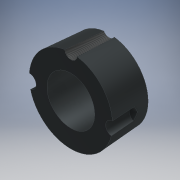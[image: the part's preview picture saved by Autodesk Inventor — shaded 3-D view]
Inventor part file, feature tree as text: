
AUTODESK INVENTOR PART (.ipt)
format: ipt  version: 2018 (Build 220112000, 112)  size: 166,400 bytes
history: native  units: mm
features: sketch x7, extrude x5, hole x2, other x2
ambient origin geometry x8: Origin, YZ Plane, XZ Plane, XY Plane, X Axis, Y Axis, Z Axis, Center Point
bodies: Solido1 (feature_tree)
feature tree (16):
  extrude  "Estrusione1"  Depth=30.0mm
  extrude  "Estrusione2"  Depth=80.0mm
  hole  "Foro1"  [1 undecoded]
  hole  "Foro2"  [1 undecoded]
  extrude  "Estrusione3"  Depth=34.0mm TaperAngle=0.0deg
  extrude  "Estrusione4"  Depth=69.77mm
  extrude  "Estrusione5"  Depth=16.580628mm
  other  "Sformo faccia1"
  sketch  "Schizzo1"
  sketch  "Schizzo2"
  sketch  "Schizzo3"
  sketch  "Schizzo4"
  sketch  "Schizzo5"
  sketch  "Schizzo6"
  other  "Linea chiusa proiettata1"
  sketch  "Schizzo7"
note: 2 required parameter values undecoded (feature->parameter linkage not recoverable at this tier; creation-order binding heuristic only, values carry confidence <= 0.55)
